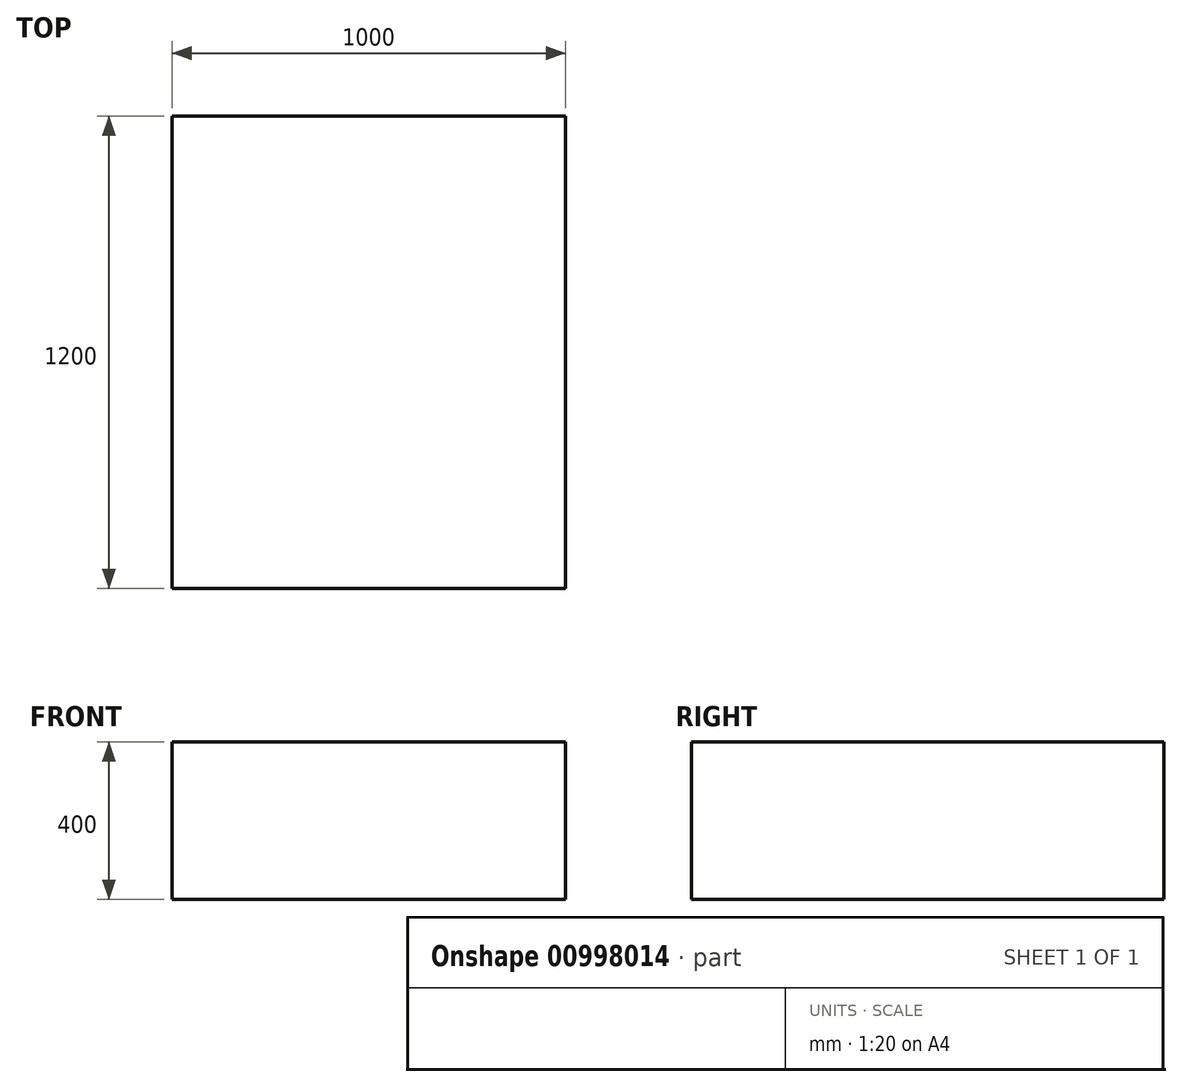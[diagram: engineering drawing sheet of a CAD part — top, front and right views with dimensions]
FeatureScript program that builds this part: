
annotation { "Feature Type Name" : "Feature", "Feature Type Description" : "" }
export const myFeature = defineFeature(function(context is Context, id is Id, definition is map)
    precondition{}
    {
        {
            var Q0;
            Q0=qCreatedBy(makeId("Top.planeOp"),FACE);
            var sketch = newSketch(context, id + "F0", { "sketchPlane" : qUnion([Q0])});
            skLineSegment(sketch, "E0", {"start": v(0, 0) * mm, "end": v(0, 898.63) * mm, "construction": true});
            skLineSegment(sketch, "E1", {"start": v(0, 0) * mm, "end": v(-884.97, 0) * mm, "construction": true});
            skLineSegment(sketch, "E2.bottom", {"start": v(-500, 600) * mm, "end": v(500, 600) * mm});
            skLineSegment(sketch, "E2.top", {"start": v(-500, -600) * mm, "end": v(500, -600) * mm});
            skLineSegment(sketch, "E2.left", {"start": v(-500, 600) * mm, "end": v(-500, -600) * mm});
            skLineSegment(sketch, "E2.right", {"start": v(500, 600) * mm, "end": v(500, -600) * mm});
            skSolve(sketch);
        }
        {
            var Q0;
            Q0 = qSketchRegion(id + "F0", true);
            extrude(context, id + "F1", {"entities" : qUnion([Q0]), "depth" : 400 * mm, "offsetDistance" : 25 * mm});
        }
    });
